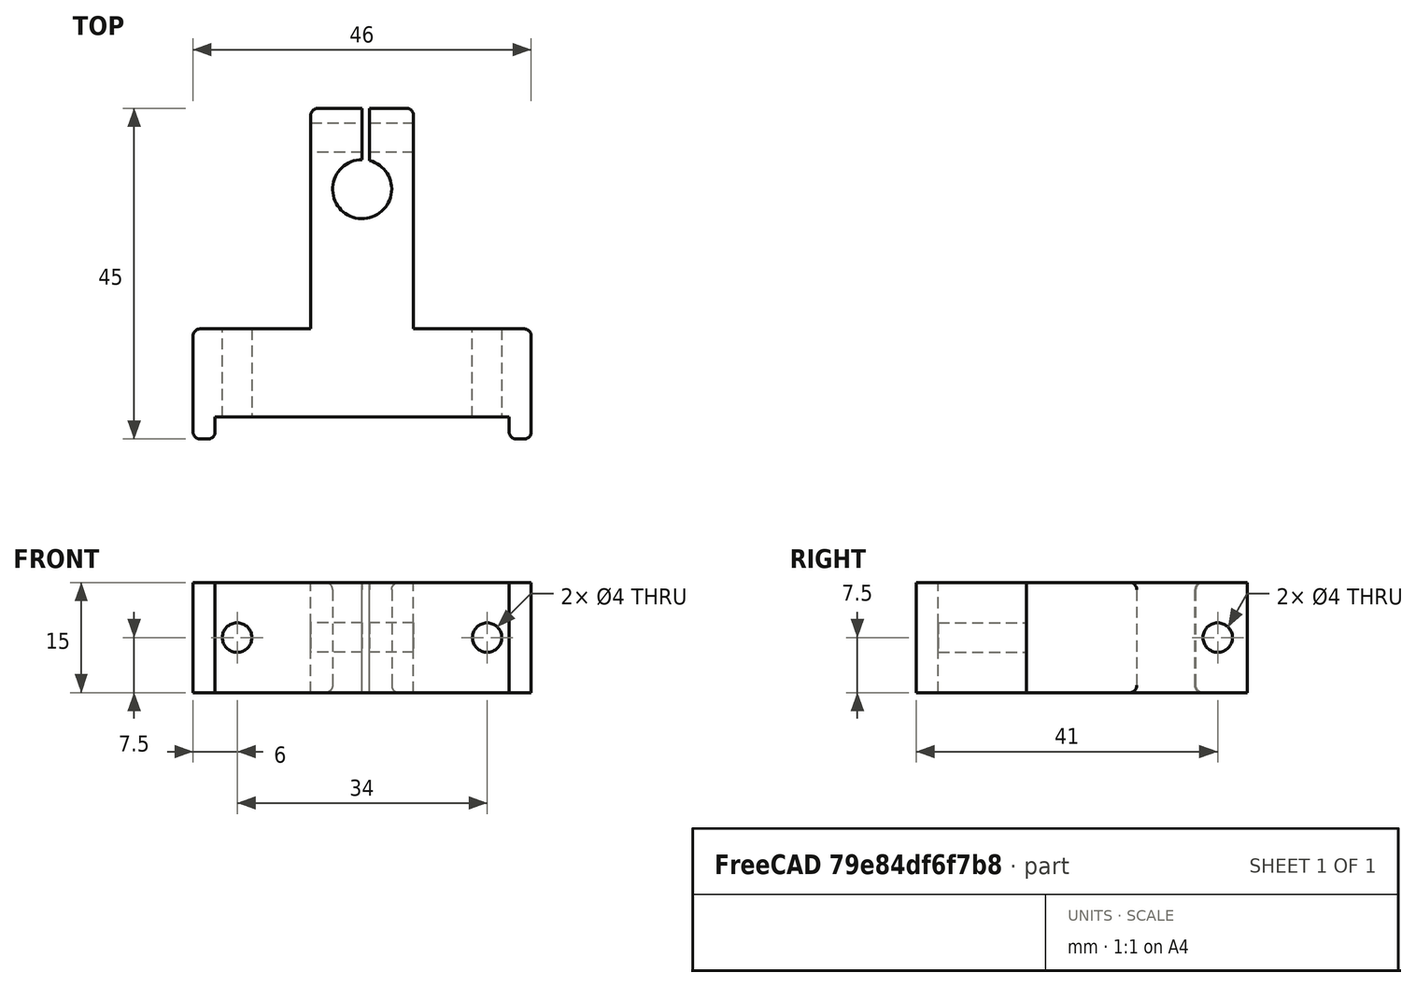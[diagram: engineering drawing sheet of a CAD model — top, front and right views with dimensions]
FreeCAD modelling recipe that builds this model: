
FCSTD DOCUMENT  (FreeCAD 0.16R)
Label: Soporte_Guias
License: All rights reserved
LicenseURL: http://en.wikipedia.org/wiki/All_rights_reserved
objects: Sketcher::SketchObject×3, PartDesign::Pad×3, Part::Cut×2, PartDesign::Fillet×1
note: 12 computed .brp shape members not serialized (recipe doc carries the construction recipe); baked Part::Feature solids carry a one-line shape summary decoded from their .brp

FEATURE [Sketcher::SketchObject] Sketch
  sketch-geometry (17):
    g0: LineSegment StartX=0 StartY=0 StartZ=0 EndX=20 EndY=0 EndZ=0
    g1: LineSegment StartX=20 StartY=0 StartZ=0 EndX=20 EndY=-3 EndZ=0
    g2: LineSegment StartX=20 StartY=-3 StartZ=0 EndX=23 EndY=-3 EndZ=0
    g3: LineSegment StartX=23 StartY=-3 StartZ=0 EndX=23 EndY=12 EndZ=0
    g4: LineSegment StartX=23 StartY=12 StartZ=0 EndX=7 EndY=12 EndZ=0
    g5: LineSegment StartX=7 StartY=12 StartZ=0 EndX=7 EndY=42 EndZ=0
    g6: LineSegment StartX=-7 StartY=42 StartZ=0 EndX=-7 EndY=12 EndZ=0
    g7: LineSegment StartX=-7 StartY=12 StartZ=0 EndX=-23 EndY=12 EndZ=0
    g8: LineSegment StartX=0 StartY=0 StartZ=0 EndX=-20 EndY=0 EndZ=0
    g9: LineSegment StartX=-20 StartY=0 StartZ=0 EndX=-20 EndY=-3 EndZ=0
    g10: LineSegment StartX=-20 StartY=-3 StartZ=0 EndX=-23 EndY=-3 EndZ=0
    g11: LineSegment StartX=-23 StartY=-3 StartZ=0 EndX=-23 EndY=12 EndZ=0
    g12: ArcOfCircle CenterX=0.00169095 CenterY=31.008 CenterZ=0 NormalX=0 NormalY=0 NormalZ=1 Radius=4.01865 StartAngle=1.57122 EndAngle=7.60337
    g13: LineSegment StartX=-7 StartY=42 StartZ=0 EndX=0 EndY=42 EndZ=0
    g14: LineSegment StartX=0.998309 StartY=42 StartZ=0 EndX=7 EndY=42 EndZ=0
    g15: LineSegment StartX=0 StartY=42 StartZ=0 EndX=0 EndY=35.0266 EndZ=0
    g16: LineSegment StartX=0.998309 StartY=34.9011 StartZ=0 EndX=0.998309 EndY=42 EndZ=0
FEATURE [Sketcher::SketchObject] Sketch001
  Placement = pos=(0,0,0) rot=(1,0,0;1.5708rad)
  sketch-geometry (2):
    g0: Circle CenterX=-17 CenterY=0 CenterZ=0 NormalX=0 NormalY=0 NormalZ=1 Radius=2
    g1: Circle CenterX=17 CenterY=0 CenterZ=0 NormalX=0 NormalY=0 NormalZ=1 Radius=2
  constraints (1):
    c: PointOnObject(g1,g-1)
FEATURE [PartDesign::Pad] Pad001
  Length = 40
  Length2 = 100
  Midplane = true
  Placement = pos=(0,0,0) rot=(1,0,0;1.5708rad)
  Sketch = -> Sketch001
  Type = 0
FEATURE [Sketcher::SketchObject] Sketch002
  Placement = pos=(0,0,0) rot=(0.57735,0.57735,0.57735;2.0944rad)
  sketch-geometry (1):
    g0: Circle CenterX=38 CenterY=0 CenterZ=0 NormalX=0 NormalY=0 NormalZ=1 Radius=2
  constraints (1):
    c: PointOnObject(g0,g-1)
FEATURE [PartDesign::Pad] Pad002
  Length = 35
  Length2 = 100
  Midplane = true
  Placement = pos=(0,0,0) rot=(0.57735,0.57735,0.57735;2.0944rad)
  Sketch = -> Sketch002
  Type = 0
FEATURE [PartDesign::Pad] Pad
  Length = 15
  Length2 = 100
  Midplane = true
  Sketch = -> Sketch
  Type = 0
FEATURE [Part::Cut] Cut
  Base = -> Pad
  Tool = -> Pad001
FEATURE [Part::Cut] Cut001
  Base = -> Cut
  Tool = -> Pad002
FEATURE [PartDesign::Fillet] Fillet
  Base = -> Cut001 [Edge46,Edge43,Edge40,Edge61,Edge47,Edge49,Edge32,Edge60,Edge57,Edge17]
  Radius = 1
